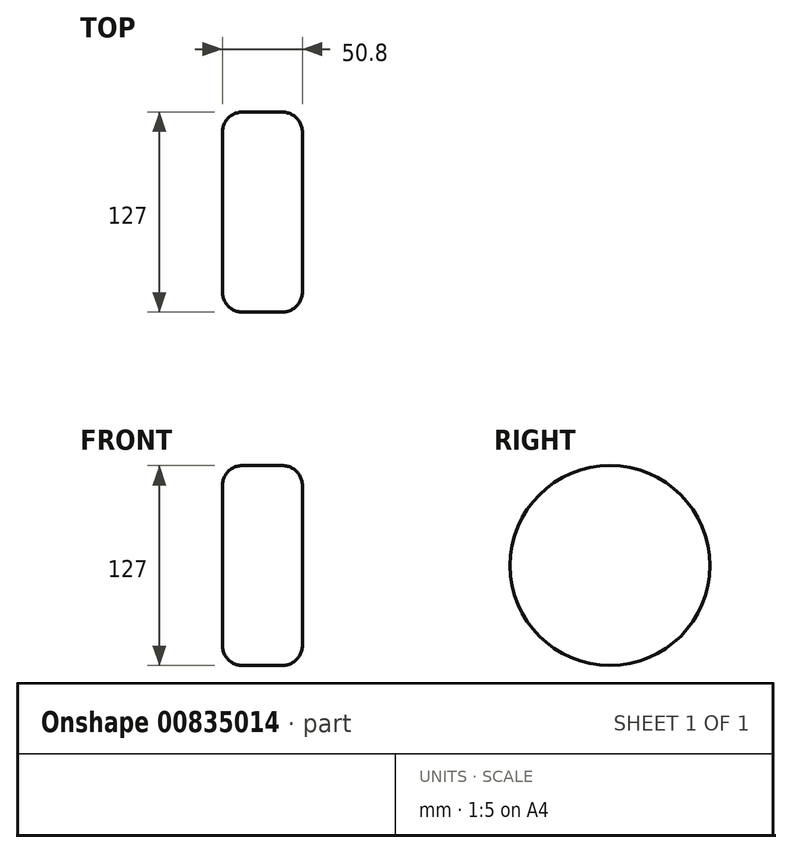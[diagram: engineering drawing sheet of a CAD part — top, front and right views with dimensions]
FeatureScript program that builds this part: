
annotation { "Feature Type Name" : "Feature", "Feature Type Description" : "" }
export const myFeature = defineFeature(function(context is Context, id is Id, definition is map)
    precondition{}
    {
        {
            var Q0;
            Q0=qCreatedBy(makeId("Right.planeOp"),FACE);
            var sketch = newSketch(context, id + "F0", { "sketchPlane" : qUnion([Q0])});
            skCircle(sketch, "E0", {"center": v(0, 0) * mm, "radius": 63.5 * mm});
            skCircle(sketch, "E1", {"center": v(0, 0) * mm, "radius": 38.1 * mm, "construction": true});
            skLineSegment(sketch, "E2.bottom", {"start": v(26.23, 27.63) * mm, "end": v(-26.23, 27.63) * mm, "construction": true});
            skLineSegment(sketch, "E2.top", {"start": v(26.23, -27.63) * mm, "end": v(-26.23, -27.63) * mm, "construction": true});
            skLineSegment(sketch, "E2.left", {"start": v(26.23, 27.63) * mm, "end": v(26.23, -27.63) * mm, "construction": true});
            skLineSegment(sketch, "E2.right", {"start": v(-26.23, 27.63) * mm, "end": v(-26.23, -27.63) * mm, "construction": true});
            skLineSegment(sketch, "E3", {"start": v(-26.23, 27.63) * mm, "end": v(26.23, -27.63) * mm});
            skLineSegment(sketch, "E4", {"start": v(26.23, 27.63) * mm, "end": v(-26.23, -27.63) * mm});
            skLineSegment(sketch, "E5", {"start": v(0, 38.1) * mm, "end": v(0, -38.1) * mm});
            skLineSegment(sketch, "E6", {"start": v(-38.1, 0) * mm, "end": v(38.1, 0) * mm});
            skSolve(sketch);
        }
        {
            var Q0;
            Q0=makeQuery(id+"F0.imprint","IMPRINT",FACE,{"disambiguationData":[TD([[makeQuery(id+"F0.imprint","IMPRINT",EDGE,{"derivedFrom":sQuery(id+"F0.wireOp",EDGE,"E0")}),1.0]])]});
            extrude(context, id + "F1", {"entities" : qUnion([Q0]), "endBound" : BoundingType.SYMMETRIC, "depth" : 50.8 * mm, "offsetDistance" : 25.4 * mm});
        }
        {
            var Q0;
            Q0=makeQuery(id+"F1.opExtrude","CAP_EDGE",EDGE,{"disambiguationData":[OSD([sQuery(id+"F0.wireOp",EDGE,"E0")])],"isStart":false});
            var Q1;
            Q1=makeQuery(id+"F1.opExtrude","CAP_EDGE",EDGE,{"disambiguationData":[OSD([sQuery(id+"F0.wireOp",EDGE,"E0")])],"isStart":true});
            fillet(context, id + "F2", {"entities" : qUnion([Q0, Q1]), "radius" : 12.7 * mm, "tangentPropagation" : true, "allowEdgeOverflow" : false});
        }
    });
